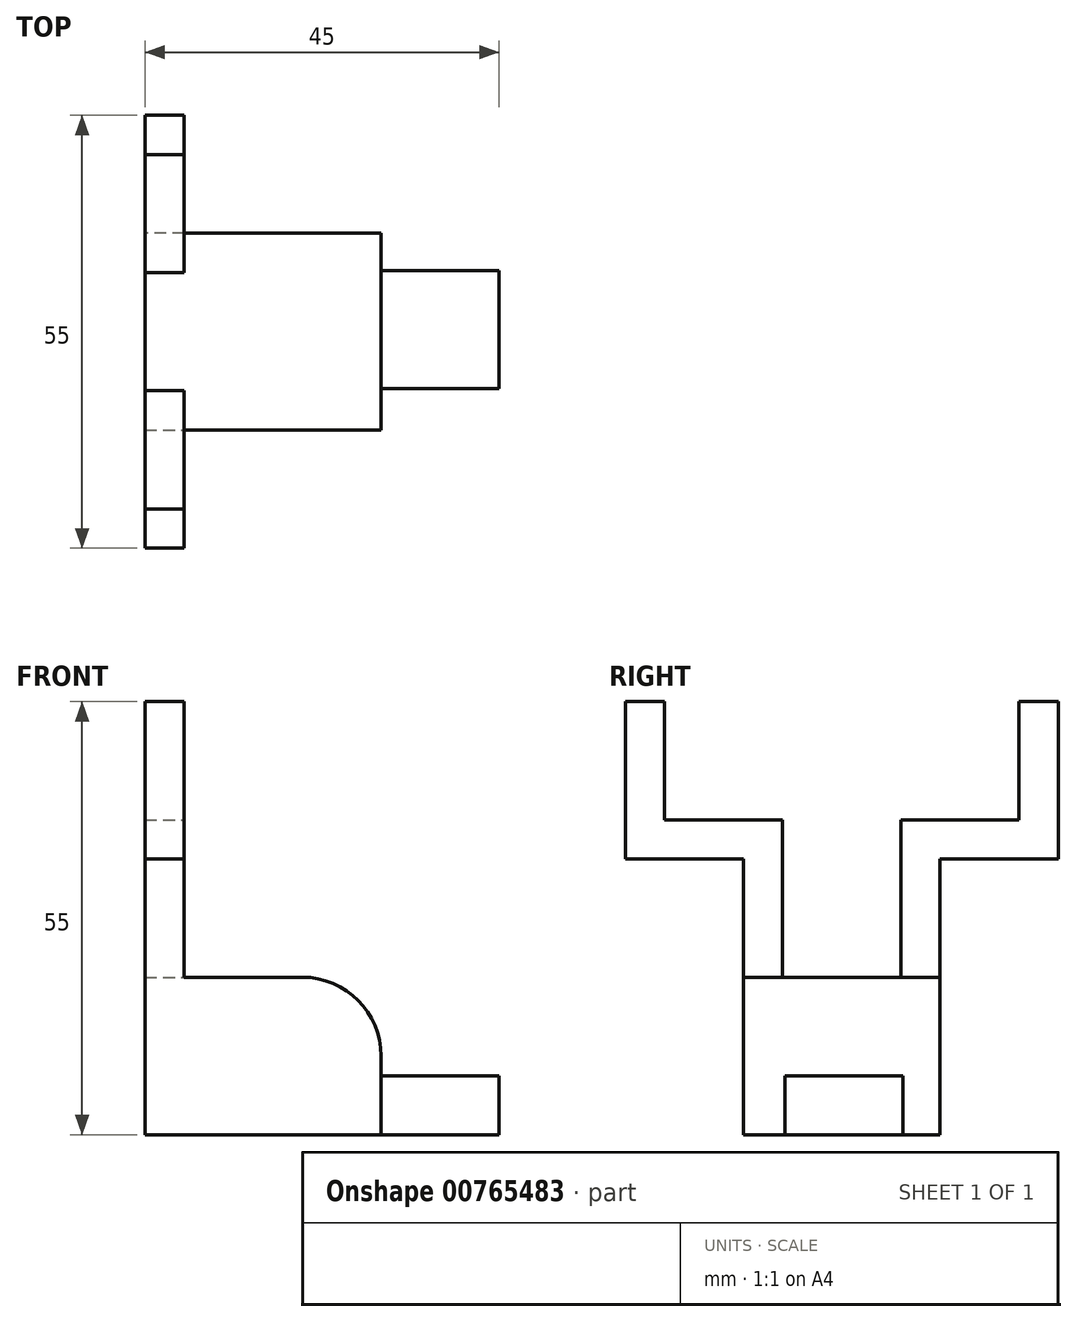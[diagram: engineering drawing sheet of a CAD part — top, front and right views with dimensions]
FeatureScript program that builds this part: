
annotation { "Feature Type Name" : "Feature", "Feature Type Description" : "" }
export const myFeature = defineFeature(function(context is Context, id is Id, definition is map)
    precondition{}
    {
        {
            var Q0;
            Q0=qCreatedBy(makeId("Top.planeOp"),FACE);
            var sketch = newSketch(context, id + "F0", { "sketchPlane" : qUnion([Q0])});
            skLineSegment(sketch, "E0.bottom", {"start": v(-57.37, -41.74) * mm, "end": v(-27.37, -41.74) * mm});
            skLineSegment(sketch, "E0.top", {"start": v(-57.37, -16.74) * mm, "end": v(-27.37, -16.74) * mm});
            skLineSegment(sketch, "E0.left", {"start": v(-57.37, -41.74) * mm, "end": v(-57.37, -16.74) * mm});
            skLineSegment(sketch, "E0.right", {"start": v(-27.37, -41.74) * mm, "end": v(-27.37, -16.74) * mm});
            skSolve(sketch);
        }
        {
            var Q0;
            Q0=makeQuery(id+"F0.imprint","IMPRINT",FACE,{"disambiguationData":[TD([[makeQuery(id+"F0.imprint","IMPRINT",EDGE,{"derivedFrom":sQuery(id+"F0.wireOp",EDGE,"E0.bottom")}),1.0]])]});
            extrude(context, id + "F1", {"entities" : qUnion([Q0]), "depth" : 20 * mm, "offsetDistance" : 25 * mm});
        }
        {
            var Q0;
            Q0=makeQuery(id+"F1.opExtrude","SWEPT_FACE",FACE,{"disambiguationData":[OSD([sQuery(id+"F0.wireOp",EDGE,"E0.right")])]});
            var sketch = newSketch(context, id + "F2", { "sketchPlane" : qUnion([Q0])});
            skLineSegment(sketch, "E1.bottom", {"start": v(-36.45, 0) * mm, "end": v(-21.45, 0) * mm});
            skLineSegment(sketch, "E1.top", {"start": v(-36.45, 7.5) * mm, "end": v(-21.45, 7.5) * mm});
            skLineSegment(sketch, "E1.left", {"start": v(-36.45, 0) * mm, "end": v(-36.45, 7.5) * mm});
            skLineSegment(sketch, "E1.right", {"start": v(-21.45, 0) * mm, "end": v(-21.45, 7.5) * mm});
            skSolve(sketch);
        }
        {
            var Q0;
            Q0=makeQuery(id+"F2.imprint","IMPRINT",FACE,{"disambiguationData":[TD([[makeQuery(id+"F2.imprint","IMPRINT",EDGE,{"derivedFrom":sQuery(id+"F2.wireOp",EDGE,"E1.bottom")}),1.0]])]});
            extrude(context, id + "F3", {"entities" : qUnion([Q0]), "operationType" : NewBodyOperationType.ADD, "depth" : 15 * mm, "offsetDistance" : 25 * mm});
        }
        {
            var Q0;
            Q0=makeQuery(id+"F1.opExtrude","CAP_FACE",FACE,{"disambiguationData":[OSD([sQuery(id+"F0.wireOp",EDGE,"E0.bottom"),sQuery(id+"F0.wireOp",EDGE,"E0.top"),sQuery(id+"F0.wireOp",EDGE,"E0.left"),sQuery(id+"F0.wireOp",EDGE,"E0.right")])],"isStart":false});
            var sketch = newSketch(context, id + "F4", { "sketchPlane" : qUnion([Q0])});
            skLineSegment(sketch, "E2.bottom", {"start": v(-57.37, -16.74) * mm, "end": v(-52.37, -16.74) * mm});
            skLineSegment(sketch, "E2.top", {"start": v(-57.37, -21.74) * mm, "end": v(-52.37, -21.74) * mm});
            skLineSegment(sketch, "E2.left", {"start": v(-57.37, -16.74) * mm, "end": v(-57.37, -21.74) * mm});
            skLineSegment(sketch, "E2.right", {"start": v(-52.37, -16.74) * mm, "end": v(-52.37, -21.74) * mm});
            skLineSegment(sketch, "E3.bottom", {"start": v(-57.37, -41.74) * mm, "end": v(-52.37, -41.74) * mm});
            skLineSegment(sketch, "E3.top", {"start": v(-57.37, -36.74) * mm, "end": v(-52.37, -36.74) * mm});
            skLineSegment(sketch, "E3.left", {"start": v(-57.37, -41.74) * mm, "end": v(-57.37, -36.74) * mm});
            skLineSegment(sketch, "E3.right", {"start": v(-52.37, -41.74) * mm, "end": v(-52.37, -36.74) * mm});
            skSolve(sketch);
        }
        {
            var Q0;
            Q0=makeQuery(id+"F4.imprint","IMPRINT",FACE,{"disambiguationData":[TD([[makeQuery(id+"F4.imprint","IMPRINT",EDGE,{"derivedFrom":sQuery(id+"F4.wireOp",EDGE,"E2.bottom")}),-1.0]])]});
            var Q1;
            Q1=makeQuery(id+"F4.imprint","IMPRINT",FACE,{"disambiguationData":[TD([[makeQuery(id+"F4.imprint","IMPRINT",EDGE,{"derivedFrom":sQuery(id+"F4.wireOp",EDGE,"E3.bottom")}),1.0]])]});
            extrude(context, id + "F5", {"entities" : qUnion([Q0, Q1]), "operationType" : NewBodyOperationType.ADD, "depth" : 20 * mm, "offsetDistance" : 25 * mm});
        }
        {
            var Q0;
            Q0=makeQuery(id+"F5.boolean.opBoolean","MERGE",FACE,{"derivedFrom":[makeQuery(id+"F1.opExtrude","SWEPT_FACE",FACE,{"disambiguationData":[OSD([sQuery(id+"F0.wireOp",EDGE,"E0.top")])]}),makeQuery(id+"F5.opExtrude","SWEPT_FACE",FACE,{"disambiguationData":[OSD([sQuery(id+"F4.wireOp",EDGE,"E2.bottom")])]})]});
            var sketch = newSketch(context, id + "F6", { "sketchPlane" : qUnion([Q0])});
            skLineSegment(sketch, "E4.bottom", {"start": v(52.37, 40) * mm, "end": v(57.37, 40) * mm});
            skLineSegment(sketch, "E4.top", {"start": v(52.37, 35) * mm, "end": v(57.37, 35) * mm});
            skLineSegment(sketch, "E4.left", {"start": v(52.37, 40) * mm, "end": v(52.37, 35) * mm});
            skLineSegment(sketch, "E4.right", {"start": v(57.37, 40) * mm, "end": v(57.37, 35) * mm});
            skSolve(sketch);
        }
        {
            var Q0;
            Q0=makeQuery(id+"F6.imprint","IMPRINT",FACE,{"disambiguationData":[TD([[makeQuery(id+"F6.imprint","IMPRINT",EDGE,{"derivedFrom":sQuery(id+"F6.wireOp",EDGE,"E4.bottom")}),1.0]])]});
            extrude(context, id + "F7", {"entities" : qUnion([Q0]), "operationType" : NewBodyOperationType.ADD, "depth" : 15 * mm, "offsetDistance" : 25 * mm});
        }
        {
            var Q0;
            Q0=makeQuery(id+"F5.boolean.opBoolean","MERGE",FACE,{"derivedFrom":[makeQuery(id+"F1.opExtrude","SWEPT_FACE",FACE,{"disambiguationData":[OSD([sQuery(id+"F0.wireOp",EDGE,"E0.bottom")])]}),makeQuery(id+"F5.opExtrude","SWEPT_FACE",FACE,{"disambiguationData":[OSD([sQuery(id+"F4.wireOp",EDGE,"E3.bottom")])]})]});
            var sketch = newSketch(context, id + "F8", { "sketchPlane" : qUnion([Q0])});
            skLineSegment(sketch, "E5.bottom", {"start": v(-57.37, 40) * mm, "end": v(-52.37, 40) * mm});
            skLineSegment(sketch, "E5.top", {"start": v(-57.37, 35) * mm, "end": v(-52.37, 35) * mm});
            skLineSegment(sketch, "E5.left", {"start": v(-57.37, 40) * mm, "end": v(-57.37, 35) * mm});
            skLineSegment(sketch, "E5.right", {"start": v(-52.37, 40) * mm, "end": v(-52.37, 35) * mm});
            skSolve(sketch);
        }
        {
            var Q0;
            Q0=makeQuery(id+"F8.imprint","IMPRINT",FACE,{"disambiguationData":[TD([[makeQuery(id+"F8.imprint","IMPRINT",EDGE,{"derivedFrom":sQuery(id+"F8.wireOp",EDGE,"E5.bottom")}),-1.0]])]});
            extrude(context, id + "F9", {"entities" : qUnion([Q0]), "operationType" : NewBodyOperationType.ADD, "depth" : 15 * mm, "offsetDistance" : 25 * mm});
        }
        {
            var Q0;
            Q0=makeQuery(id+"F7.boolean.opBoolean","MERGE",FACE,{"derivedFrom":[makeQuery(id+"F5.opExtrude","CAP_FACE",FACE,{"disambiguationData":[OSD([sQuery(id+"F4.wireOp",EDGE,"E2.bottom"),sQuery(id+"F4.wireOp",EDGE,"E2.top"),sQuery(id+"F4.wireOp",EDGE,"E2.left"),sQuery(id+"F4.wireOp",EDGE,"E2.right")])],"isStart":false}),makeQuery(id+"F7.opExtrude","SWEPT_FACE",FACE,{"disambiguationData":[OSD([sQuery(id+"F6.wireOp",EDGE,"E4.bottom")])]})]});
            var sketch = newSketch(context, id + "F10", { "sketchPlane" : qUnion([Q0])});
            skLineSegment(sketch, "E6.bottom", {"start": v(-57.37, -1.74) * mm, "end": v(-52.37, -1.74) * mm});
            skLineSegment(sketch, "E6.top", {"start": v(-57.37, -6.74) * mm, "end": v(-52.37, -6.74) * mm});
            skLineSegment(sketch, "E6.left", {"start": v(-57.37, -1.74) * mm, "end": v(-57.37, -6.74) * mm});
            skLineSegment(sketch, "E6.right", {"start": v(-52.37, -1.74) * mm, "end": v(-52.37, -6.74) * mm});
            skSolve(sketch);
        }
        {
            var Q0;
            Q0=makeQuery(id+"F9.boolean.opBoolean","MERGE",FACE,{"derivedFrom":[makeQuery(id+"F5.opExtrude","CAP_FACE",FACE,{"disambiguationData":[OSD([sQuery(id+"F4.wireOp",EDGE,"E3.bottom"),sQuery(id+"F4.wireOp",EDGE,"E3.top"),sQuery(id+"F4.wireOp",EDGE,"E3.left"),sQuery(id+"F4.wireOp",EDGE,"E3.right")])],"isStart":false}),makeQuery(id+"F9.opExtrude","SWEPT_FACE",FACE,{"disambiguationData":[OSD([sQuery(id+"F8.wireOp",EDGE,"E5.bottom")])]})]});
            var sketch = newSketch(context, id + "F11", { "sketchPlane" : qUnion([Q0])});
            skLineSegment(sketch, "E7.bottom", {"start": v(-57.37, -56.74) * mm, "end": v(-52.37, -56.74) * mm});
            skLineSegment(sketch, "E7.top", {"start": v(-57.37, -51.74) * mm, "end": v(-52.37, -51.74) * mm});
            skLineSegment(sketch, "E7.left", {"start": v(-57.37, -56.74) * mm, "end": v(-57.37, -51.74) * mm});
            skLineSegment(sketch, "E7.right", {"start": v(-52.37, -56.74) * mm, "end": v(-52.37, -51.74) * mm});
            skSolve(sketch);
        }
        {
            var Q0;
            Q0=makeQuery(id+"F10.imprint","IMPRINT",FACE,{"disambiguationData":[TD([[makeQuery(id+"F10.imprint","IMPRINT",EDGE,{"derivedFrom":sQuery(id+"F10.wireOp",EDGE,"E6.bottom")}),-1.0]])]});
            var Q1;
            Q1=makeQuery(id+"F11.imprint","IMPRINT",FACE,{"disambiguationData":[TD([[makeQuery(id+"F11.imprint","IMPRINT",EDGE,{"derivedFrom":sQuery(id+"F11.wireOp",EDGE,"E7.bottom")}),1.0]])]});
            extrude(context, id + "F12", {"entities" : qUnion([Q0, Q1]), "operationType" : NewBodyOperationType.ADD, "depth" : 15 * mm, "offsetDistance" : 25 * mm});
        }
        {
            var Q0;
            Q0=makeQuery(id+"F1.opExtrude","CAP_EDGE",EDGE,{"disambiguationData":[OSD([sQuery(id+"F0.wireOp",EDGE,"E0.right")])],"isStart":false});
            fillet(context, id + "F13", {"entities" : qUnion([Q0]), "radius" : 10 * mm, "tangentPropagation" : true, "allowEdgeOverflow" : false});
        }
    });
